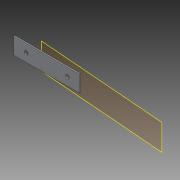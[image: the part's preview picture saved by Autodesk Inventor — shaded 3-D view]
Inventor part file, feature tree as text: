
AUTODESK INVENTOR PART (.ipt)
format: ipt  version: 2014 SP1 (Build 180222100, 222)  size: 83,968 bytes
history: native  units: in
note: dims shown in document units (in); Inventor stores cm internally (conversion verified against a paired STEP export)
features: extrude x2, sketch x2, plane x1, reference x1
ambient origin geometry x8: Origin, YZ Plane, XZ Plane, XY Plane, X Axis, Y Axis, Z Axis, Center Point
bodies: Solid1 (feature_tree)
feature tree (6):
  extrude  "Extrusion1"  Depth=2.0in
  plane  "Work Plane2"
  extrude  "Extrusion2"  Depth=0.0312in
  sketch  "Sketch1"  dims[d0=0.5in d1=2.0in]
  sketch  "Sketch2"  dims[d2=0.125in d3=0.375in d4=0.0312in d5=0.0in d7=1.0in d8=0.0in]
  reference  "Reference1"
